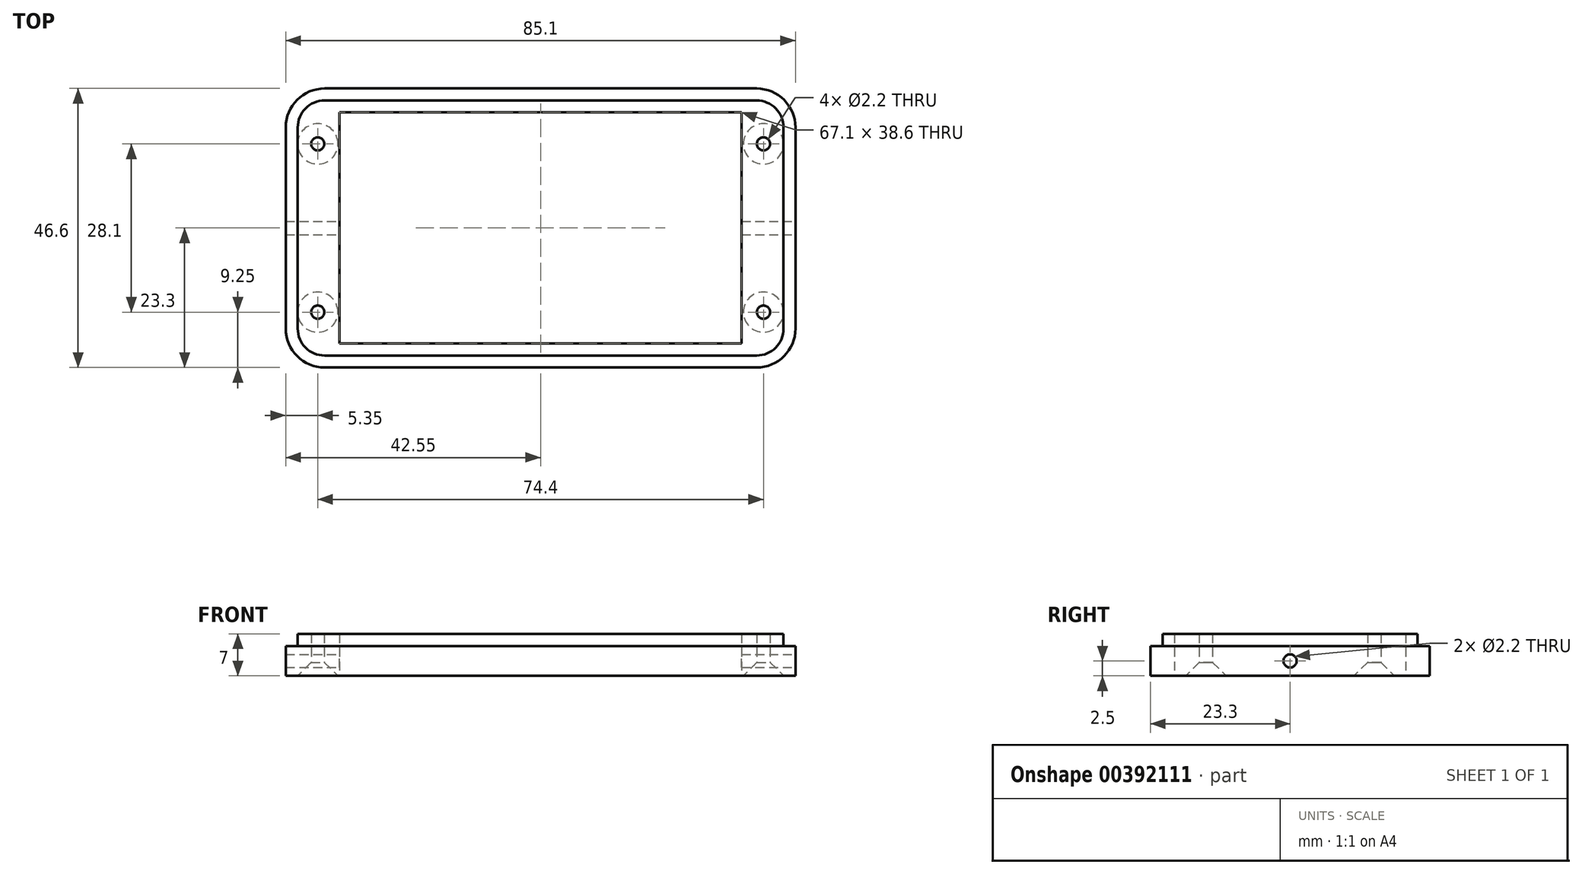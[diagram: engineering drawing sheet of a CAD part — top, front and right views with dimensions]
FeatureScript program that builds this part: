
annotation { "Feature Type Name" : "Feature", "Feature Type Description" : "" }
export const myFeature = defineFeature(function(context is Context, id is Id, definition is map)
    precondition{}
    {
        {
            var Q0;
            Q0=qCreatedBy(makeId("Top.planeOp"),FACE);
            var sketch = newSketch(context, id + "F0", { "sketchPlane" : qUnion([Q0])});
            skLineSegment(sketch, "E0.bottom", {"start": v(36.05, 21.3) * mm, "end": v(-36.05, 21.3) * mm});
            skLineSegment(sketch, "E0.top", {"start": v(36.05, -21.3) * mm, "end": v(-36.05, -21.3) * mm});
            skLineSegment(sketch, "E0.left", {"start": v(40.55, 16.8) * mm, "end": v(40.55, -16.8) * mm});
            skLineSegment(sketch, "E0.right", {"start": v(-40.55, 16.8) * mm, "end": v(-40.55, -16.8) * mm});
            skPoint(sketch, "E0.middle", {"position": v(0, 0) * mm});
            skArc(sketch, "E1.filletArc", {"start": v(-36.05, 21.3) * mm, "mid": v(-39.23, 19.98) * mm, "end": v(-40.55, 16.8) * mm});
            skPoint(sketch, "E2.visualSharp", {"position": v(40.55, 21.3) * mm});
            skArc(sketch, "E2.filletArc", {"start": v(40.55, 16.8) * mm, "mid": v(39.23, 19.98) * mm, "end": v(36.05, 21.3) * mm});
            skPoint(sketch, "E3.visualSharp", {"position": v(40.55, -21.3) * mm});
            skArc(sketch, "E3.filletArc", {"start": v(36.05, -21.3) * mm, "mid": v(39.23, -19.98) * mm, "end": v(40.55, -16.8) * mm});
            skPoint(sketch, "E4.visualSharp", {"position": v(-40.55, -21.3) * mm});
            skArc(sketch, "E4.filletArc", {"start": v(-40.55, -16.8) * mm, "mid": v(-39.23, -19.98) * mm, "end": v(-36.05, -21.3) * mm});
            skLineSegment(sketch, "E5", {"start": v(40.55, 0) * mm, "end": v(-40.55, 0) * mm, "construction": true});
            skLineSegment(sketch, "E6", {"start": v(0, 21.3) * mm, "end": v(0, -21.3) * mm, "construction": true});
            skLineSegment(sketch, "E7.bottom", {"start": v(-37.2, 14.05) * mm, "end": v(37.2, 14.05) * mm, "construction": true});
            skLineSegment(sketch, "E7.top", {"start": v(-37.2, -14.05) * mm, "end": v(37.2, -14.05) * mm, "construction": true});
            skLineSegment(sketch, "E7.left", {"start": v(-37.2, 14.05) * mm, "end": v(-37.2, -14.05) * mm, "construction": true});
            skLineSegment(sketch, "E7.right", {"start": v(37.2, 14.05) * mm, "end": v(37.2, -14.05) * mm, "construction": true});
            skPoint(sketch, "E8", {"position": v(37.2, 14.05) * mm});
            skPoint(sketch, "E9", {"position": v(37.2, -14.05) * mm});
            skPoint(sketch, "E10", {"position": v(-37.2, -14.05) * mm});
            skPoint(sketch, "E11", {"position": v(-37.2, 14.05) * mm});
            skArc(sketch, "E12.0", {"start": v(42.55, 16.8) * mm, "mid": v(40.65, 21.4) * mm, "end": v(36.05, 23.3) * mm});
            skLineSegment(sketch, "E12.1", {"start": v(42.55, 16.8) * mm, "end": v(42.55, -16.8) * mm});
            skLineSegment(sketch, "E12.2", {"start": v(36.05, 23.3) * mm, "end": v(-36.05, 23.3) * mm});
            skArc(sketch, "E12.3", {"start": v(36.05, -23.3) * mm, "mid": v(40.65, -21.4) * mm, "end": v(42.55, -16.8) * mm});
            skArc(sketch, "E12.4", {"start": v(-36.05, 23.3) * mm, "mid": v(-40.65, 21.4) * mm, "end": v(-42.55, 16.8) * mm});
            skLineSegment(sketch, "E12.5", {"start": v(-42.55, 16.8) * mm, "end": v(-42.55, -16.8) * mm});
            skArc(sketch, "E12.6", {"start": v(-42.55, -16.8) * mm, "mid": v(-40.65, -21.4) * mm, "end": v(-36.05, -23.3) * mm});
            skLineSegment(sketch, "E12.7", {"start": v(36.05, -23.3) * mm, "end": v(-36.05, -23.3) * mm});
            skLineSegment(sketch, "E13.bottom", {"start": v(33.55, 19.3) * mm, "end": v(-33.55, 19.3) * mm});
            skLineSegment(sketch, "E13.top", {"start": v(33.55, -19.3) * mm, "end": v(-33.55, -19.3) * mm});
            skLineSegment(sketch, "E13.left", {"start": v(33.55, 19.3) * mm, "end": v(33.55, -19.3) * mm});
            skLineSegment(sketch, "E13.right", {"start": v(-33.55, 19.3) * mm, "end": v(-33.55, -19.3) * mm});
            skLineSegment(sketch, "E14.bottom", {"start": v(-11.05, 8) * mm, "end": v(-25.55, 8) * mm, "construction": true});
            skLineSegment(sketch, "E14.top", {"start": v(-11.05, -8) * mm, "end": v(-25.55, -8) * mm, "construction": true});
            skLineSegment(sketch, "E14.left", {"start": v(-11.05, 8) * mm, "end": v(-11.05, -8) * mm, "construction": true});
            skLineSegment(sketch, "E14.right", {"start": v(-25.55, 8) * mm, "end": v(-25.55, -8) * mm, "construction": true});
            skPoint(sketch, "E14.middle", {"position": v(-18.3, 0) * mm});
            skSolve(sketch);
        }
        {
            var Q0;
            Q0=makeQuery(id+"F0.imprint","IMPRINT",FACE,{"disambiguationData":[TD([[makeQuery(id+"F0.imprint","IMPRINT",EDGE,{"derivedFrom":sQuery(id+"F0.wireOp",EDGE,"E0.bottom")}),1.0]])]});
            extrude(context, id + "F1", {"entities" : qUnion([Q0]), "depth" : 7 * mm});
        }
        {
            var Q0;
            Q0 = qSketchRegion(id + "F0", true);
            extrude(context, id + "F2", {"entities" : qUnion([Q0]), "operationType" : NewBodyOperationType.ADD, "depth" : 5 * mm});
        }
        {
            var Q0;
            Q0=sQuery(id+"F0.wireOp",VERTEX,"E8");
            var Q1;
            Q1=sQuery(id+"F0.wireOp",VERTEX,"E9");
            var Q2;
            Q2=sQuery(id+"F0.wireOp",VERTEX,"E10");
            var Q3;
            Q3=sQuery(id+"F0.wireOp",VERTEX,"E11");
            var Q4;
            Q4=makeQuery(id+"F1.opExtrude","SWEPT_BODY",BODY,{"disambiguationData":[OSD([sQuery(id+"F0.wireOp",EDGE,"E0.bottom"),sQuery(id+"F0.wireOp",EDGE,"E0.top"),sQuery(id+"F0.wireOp",EDGE,"E0.left"),sQuery(id+"F0.wireOp",EDGE,"E0.right"),sQuery(id+"F0.wireOp",EDGE,"E1.filletArc"),sQuery(id+"F0.wireOp",EDGE,"E2.filletArc"),sQuery(id+"F0.wireOp",EDGE,"E3.filletArc"),sQuery(id+"F0.wireOp",EDGE,"E4.filletArc"),sQuery(id+"F0.wireOp",EDGE,"E13.bottom"),sQuery(id+"F0.wireOp",EDGE,"E13.top"),sQuery(id+"F0.wireOp",EDGE,"E13.left"),sQuery(id+"F0.wireOp",EDGE,"E13.right")])]});
            hole(context, id + "F3", {"style" : HoleStyle.C_SINK, "endStyle" : HoleEndStyle.THROUGH, "oppositeDirection" : true, "holeDiameter" : 2.2 * mm, "cSinkDiameter" : 6.72 * mm, "cSinkAngle" : 90 * degree, "isTappedThrough" : true, "tappedDepth" : 4 * mm, "tapClearance" : 0, "locations" : qUnion([Q0, Q1, Q2, Q3]), "scope" : qUnion([Q4])});
        }
        {
            var Q0;
            Q0=makeQuery(id+"F2.opExtrude","SWEPT_FACE",FACE,{"disambiguationData":[OSD([sQuery(id+"F0.wireOp",EDGE,"E12.1")])]});
            var sketch = newSketch(context, id + "F4", { "sketchPlane" : qUnion([Q0])});
            skLineSegment(sketch, "E15", {"start": v(0, 5) * mm, "end": v(0, 0) * mm, "construction": true});
            skPoint(sketch, "E16", {"position": v(0, 2.5) * mm});
            skSolve(sketch);
        }
        {
            var Q0;
            Q0=sQuery(id+"F4.wireOp",VERTEX,"E16");
            var Q1;
            Q1=makeQuery(id+"F1.opExtrude","SWEPT_BODY",BODY,{"disambiguationData":[OSD([sQuery(id+"F0.wireOp",EDGE,"E0.bottom"),sQuery(id+"F0.wireOp",EDGE,"E0.top"),sQuery(id+"F0.wireOp",EDGE,"E0.left"),sQuery(id+"F0.wireOp",EDGE,"E0.right"),sQuery(id+"F0.wireOp",EDGE,"E1.filletArc"),sQuery(id+"F0.wireOp",EDGE,"E2.filletArc"),sQuery(id+"F0.wireOp",EDGE,"E3.filletArc"),sQuery(id+"F0.wireOp",EDGE,"E4.filletArc"),sQuery(id+"F0.wireOp",EDGE,"E13.bottom"),sQuery(id+"F0.wireOp",EDGE,"E13.top"),sQuery(id+"F0.wireOp",EDGE,"E13.left"),sQuery(id+"F0.wireOp",EDGE,"E13.right")])]});
            hole(context, id + "F5", {"style" : HoleStyle.SIMPLE, "endStyle" : HoleEndStyle.THROUGH, "holeDiameter" : 2.2 * mm, "isTappedThrough" : true, "tappedDepth" : 4 * mm, "tapClearance" : 0, "locations" : qUnion([Q0]), "scope" : qUnion([Q1])});
        }
    });
